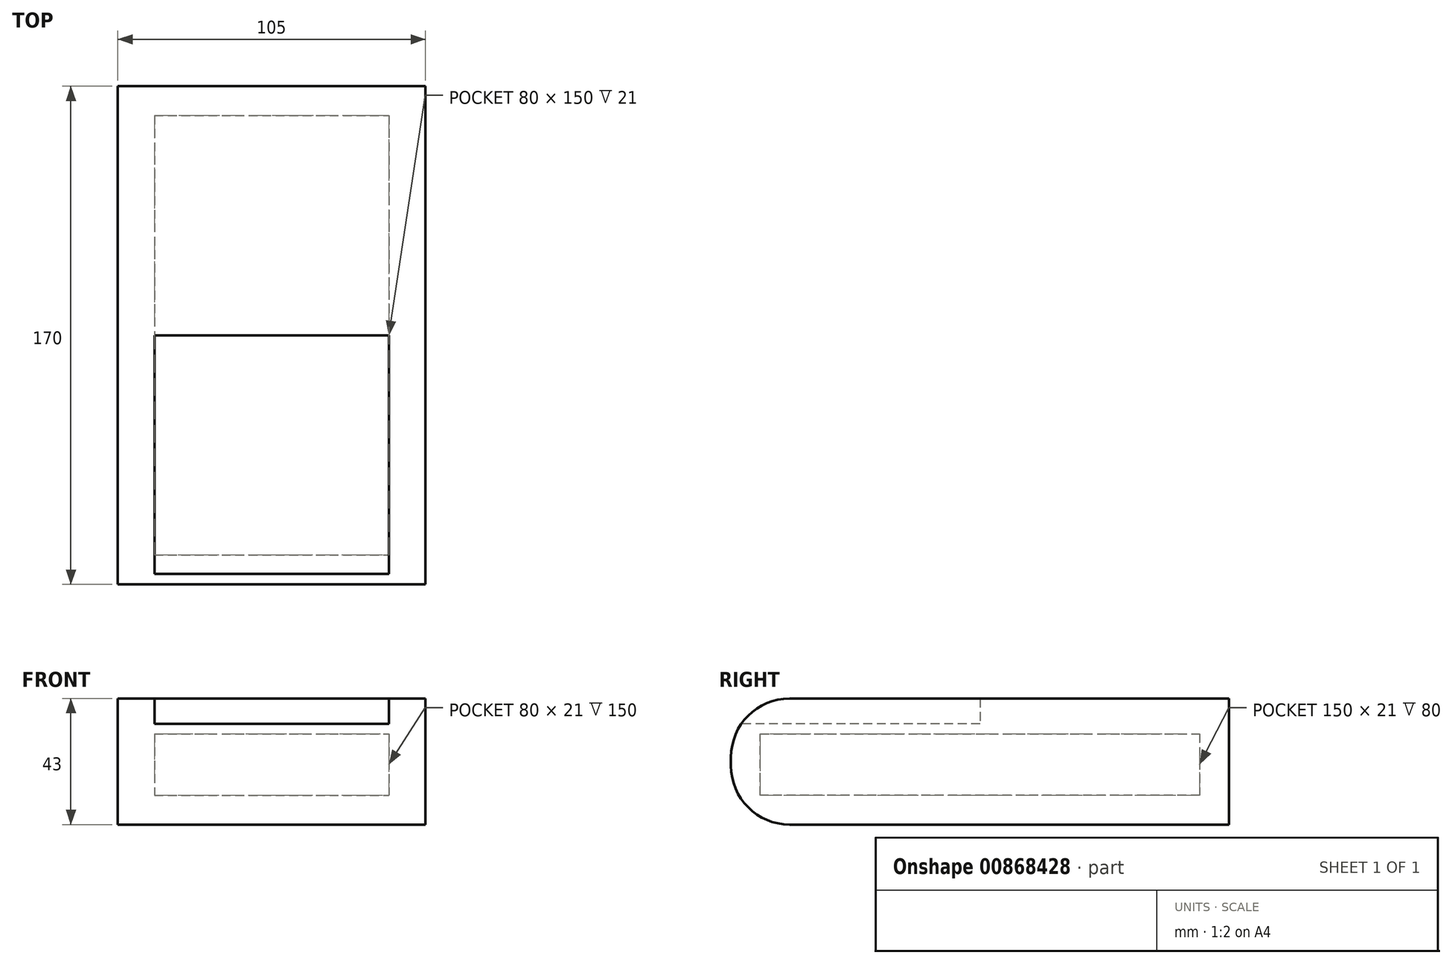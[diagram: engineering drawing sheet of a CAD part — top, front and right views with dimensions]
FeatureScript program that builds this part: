
annotation { "Feature Type Name" : "Feature", "Feature Type Description" : "" }
export const myFeature = defineFeature(function(context is Context, id is Id, definition is map)
    precondition{}
    {
        {
            var Q0;
            Q0=qCreatedBy(makeId("Right.planeOp"),FACE);
            var sketch = newSketch(context, id + "F0", { "sketchPlane" : qUnion([Q0])});
            skLineSegment(sketch, "E0.bottom", {"start": v(-85, 1.5) * mm, "end": v(85, 1.5) * mm});
            skLineSegment(sketch, "E0.top", {"start": v(-85, -1.5) * mm, "end": v(85, -1.5) * mm});
            skLineSegment(sketch, "E0.left", {"start": v(-85, 1.5) * mm, "end": v(-85, -1.5) * mm});
            skLineSegment(sketch, "E0.right", {"start": v(85, 1.5) * mm, "end": v(85, -1.5) * mm});
            skPoint(sketch, "E0.middle", {"position": v(0, 0) * mm});
            skLineSegment(sketch, "E1", {"start": v(-85, 1.5) * mm, "end": v(-85, 1.5) * mm});
            skLineSegment(sketch, "E2", {"start": v(-85, -1.5) * mm, "end": v(-85, -1.5) * mm});
            skLineSegment(sketch, "E3", {"start": v(85, 1.5) * mm, "end": v(85, 21.5) * mm});
            skLineSegment(sketch, "E4", {"start": v(85, 21.5) * mm, "end": v(-65, 21.5) * mm});
            skLineSegment(sketch, "E5", {"start": v(85, -1.5) * mm, "end": v(85, -21.5) * mm});
            skLineSegment(sketch, "E6", {"start": v(85, -21.5) * mm, "end": v(-65, -21.5) * mm});
            skPoint(sketch, "E7.visualSharp", {"position": v(-85, 21.5) * mm});
            skArc(sketch, "E7.filletArc", {"start": v(-65, 21.5) * mm, "mid": v(-79.14, 15.64) * mm, "end": v(-85, 1.5) * mm});
            skPoint(sketch, "E8.visualSharp", {"position": v(-85, -21.5) * mm});
            skArc(sketch, "E8.filletArc", {"start": v(-85, -1.5) * mm, "mid": v(-79.14, -15.64) * mm, "end": v(-65, -21.5) * mm});
            skSolve(sketch);
        }
        {
            var Q0;
            Q0=makeQuery(id+"F0.imprint","IMPRINT",FACE,{"disambiguationData":[TD([[makeQuery(id+"F0.imprint","IMPRINT",EDGE,{"derivedFrom":sQuery(id+"F0.wireOp",EDGE,"E0.bottom")}),1.0]])]});
            var Q1;
            Q1=makeQuery(id+"F0.imprint","IMPRINT",FACE,{"disambiguationData":[TD([[makeQuery(id+"F0.imprint","IMPRINT",EDGE,{"derivedFrom":sQuery(id+"F0.wireOp",EDGE,"E0.top")}),-1.0]])]});
            var Q2;
            Q2=makeQuery(id+"F0.imprint","IMPRINT",FACE,{"disambiguationData":[TD([[makeQuery(id+"F0.imprint","IMPRINT",EDGE,{"derivedFrom":sQuery(id+"F0.wireOp",EDGE,"E0.bottom")}),-1.0]])]});
            extrude(context, id + "F1", {"entities" : qUnion([Q0, Q1, Q2]), "endBound" : BoundingType.SYMMETRIC, "depth" : 105 * mm, "offsetDistance" : 25 * mm});
        }
        {
            var Q0;
            Q0=qCreatedBy(makeId("Right.planeOp"),FACE);
            var sketch = newSketch(context, id + "F2", { "sketchPlane" : qUnion([Q0])});
            skLineSegment(sketch, "E9", {"start": v(0, 0) * mm, "end": v(0, -1.5) * mm});
            skLineSegment(sketch, "E10", {"start": v(75, -11.5) * mm, "end": v(-75, -11.5) * mm});
            skLineSegment(sketch, "E11", {"start": v(-75, -11.5) * mm, "end": v(-75, -1.5) * mm});
            skLineSegment(sketch, "E12", {"start": v(-75, -1.5) * mm, "end": v(-75, 0) * mm});
            skLineSegment(sketch, "E13", {"start": v(-75, 0) * mm, "end": v(-75, 1.5) * mm});
            skLineSegment(sketch, "E14", {"start": v(-75, 1.5) * mm, "end": v(-75, 9.5) * mm});
            skLineSegment(sketch, "E15", {"start": v(-75, 9.5) * mm, "end": v(75, 9.5) * mm});
            skLineSegment(sketch, "E16", {"start": v(75, 9.5) * mm, "end": v(75, -11.5) * mm});
            skLineSegment(sketch, "E17", {"start": v(0, 22.92) * mm, "end": v(0, 12.92) * mm});
            skLineSegment(sketch, "E18", {"start": v(0, 12.92) * mm, "end": v(-84.38, 12.92) * mm});
            skPoint(sketch, "E19.orphan", {"position": v(85, 9.5) * mm});
            skPoint(sketch, "E20.start.orphan", {"position": v(85, -1.5) * mm});
            skLineSegment(sketch, "E21", {"start": v(0, 22.92) * mm, "end": v(-87.27, 22.92) * mm});
            skLineSegment(sketch, "E22", {"start": v(-87.27, 22.92) * mm, "end": v(-84.38, 12.92) * mm});
            skSolve(sketch);
        }
        {
            var Q0;
            Q0=makeQuery(id+"F2.imprint","IMPRINT",FACE,{"disambiguationData":[TD([[makeQuery(id+"F2.imprint","IMPRINT",EDGE,{"derivedFrom":sQuery(id+"F2.wireOp",EDGE,"E17")}),-1.0]])]});
            extrude(context, id + "F3", {"entities" : qUnion([Q0]), "operationType" : NewBodyOperationType.REMOVE, "endBound" : BoundingType.SYMMETRIC, "depth" : 80 * mm, "offsetDistance" : 25 * mm});
        }
        {
            var Q0;
            Q0 = qSketchRegion(id + "F2", true);
            extrude(context, id + "F4", {"entities" : qUnion([Q0]), "operationType" : NewBodyOperationType.REMOVE, "endBound" : BoundingType.SYMMETRIC, "oppositeDirection" : true, "depth" : 80 * mm, "offsetDistance" : 25 * mm});
        }
    });
